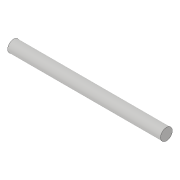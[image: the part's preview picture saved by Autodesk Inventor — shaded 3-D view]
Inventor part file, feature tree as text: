
AUTODESK INVENTOR PART (.ipt)
format: ipt  version: 2018.3 (Build 223284000, 284)  size: 70,144 bytes
history: native  units: in
note: dims shown in document units (in); Inventor stores cm internally (conversion verified against a paired STEP export)
features: extrude x1, sketch x1
ambient origin geometry x8: Origin, YZ Plane, XZ Plane, XY Plane, X Axis, Y Axis, Z Axis, Center Point
bodies: Solid1 (feature_tree)
feature tree (2):
  extrude  "Extrusion1"  Depth=3.25in TaperAngle=0.0deg
  sketch  "Sketch1"  dims[d0=0.25in d1=3.25in d2=0.0in]
